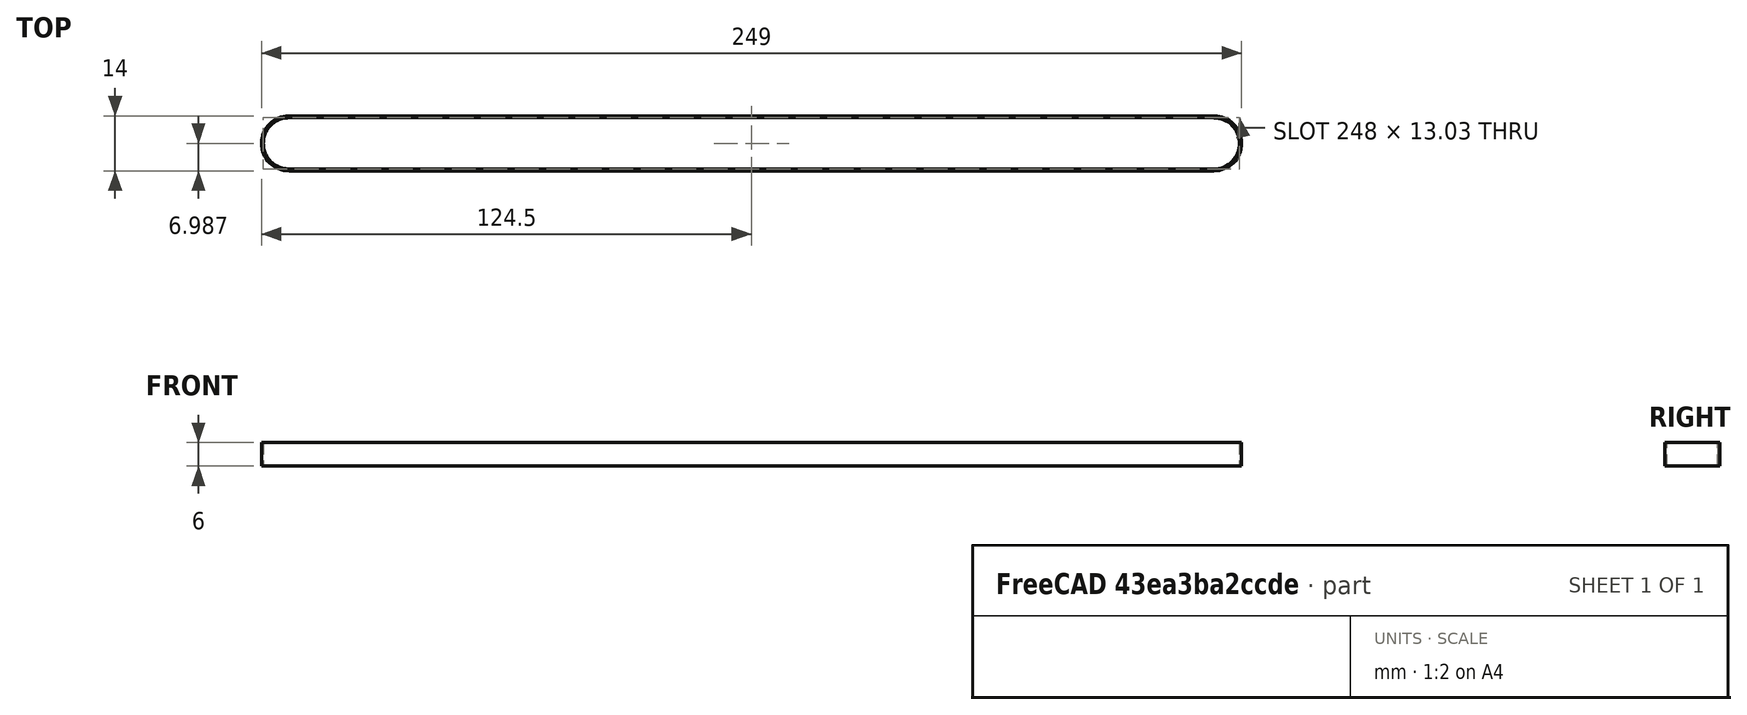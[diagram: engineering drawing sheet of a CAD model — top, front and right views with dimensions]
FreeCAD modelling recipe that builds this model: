
FCSTD DOCUMENT  (FreeCAD 0.18R16131 (Git))
Label: belt_gt2_6mm
License: All rights reserved
LicenseURL: http://en.wikipedia.org/wiki/All_rights_reserved
objects: Sketcher::SketchObject×1, PartDesign::Pad×1, PartDesign::Body×1
note: 4 computed .brp shape members not serialized (recipe doc carries the construction recipe); baked Part::Feature solids carry a one-line shape summary decoded from their .brp

FEATURE [Sketcher::SketchObject] Sketch
  MapMode = 5
  Support = -> [XY_Plane]
  sketch-geometry (8):
    g0: ArcOfCircle CenterX=0 CenterY=0 CenterZ=0 NormalX=0 NormalY=0 NormalZ=1 AngleXU=0 Radius=7 StartAngle=1.5708 EndAngle=4.71239
    g1: ArcOfCircle CenterX=235 CenterY=0 CenterZ=0 NormalX=0 NormalY=0 NormalZ=1 AngleXU=0 Radius=7 StartAngle=4.71239 EndAngle=7.85398
    g2: ArcOfCircle CenterX=0 CenterY=0 CenterZ=0 NormalX=0 NormalY=0 NormalZ=1 AngleXU=0 Radius=6.5 StartAngle=1.5706 EndAngle=4.71239
    g3: ArcOfCircle CenterX=235 CenterY=-0.0265945 CenterZ=0 NormalX=0 NormalY=0 NormalZ=1 AngleXU=0 Radius=6.5 StartAngle=4.71239 EndAngle=7.85398
    g4: LineSegment StartX=0.00126769 StartY=6.5 StartZ=0 EndX=235 EndY=6.47341 EndZ=0
    g5: LineSegment StartX=235 StartY=7 StartZ=0 EndX=-7.17788e-07 EndY=7 EndZ=0
    g6: LineSegment StartX=6.59877e-08 StartY=-7 StartZ=0 EndX=235 EndY=-7 EndZ=0
    g7: LineSegment StartX=235 StartY=-6.52659 StartZ=0 EndX=-1.5876e-06 EndY=-6.5 EndZ=0
  constraints (21):
    c: Coincident(g0,g-1)
    c: Horizontal(g0,g1)
    c: Equal(g1,g0)
    c: Radius(g0) = 7
    c: DistanceX(g0,g1) = 235
    c: Equal(g2,g3)
    c: Radius(g2) = 6.5
    c: Vertical(g1,g3)
    c: Vertical(g3,g4)
    c: Vertical(g4,g5)
    c: Vertical(g5,g6)
    c: Vertical(g6,g7)
    c: Coincident(g1,g6)
    c: Coincident(g1,g5)
    c: Coincident(g3,g4)
    c: Coincident(g3,g7)
    c: Coincident(g0,g5)
    c: Coincident(g0,g6)
    c: Coincident(g2,g4)
    c: Coincident(g2,g7)
    c: Coincident(g2,g0)
FEATURE [PartDesign::Pad] Pad
  Length = 6
  Length2 = 100
  Profile = -> Sketch
  Type = 0
FEATURE [PartDesign::Body] Body
  Group = -> [Sketch,Pad]
  Origin = -> Origin
  Tip = -> Pad
